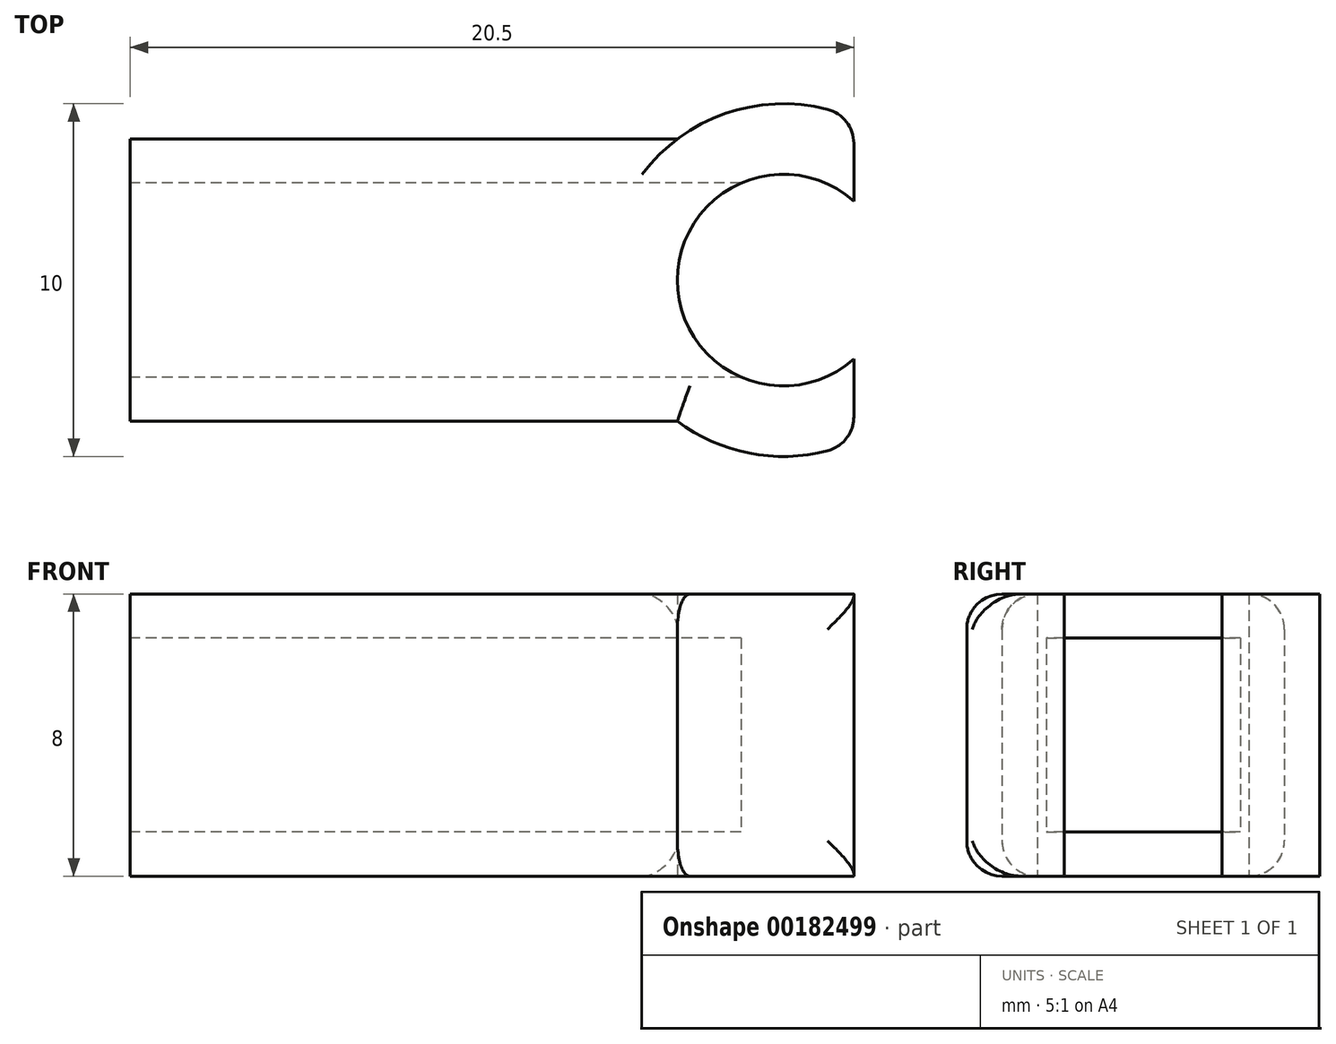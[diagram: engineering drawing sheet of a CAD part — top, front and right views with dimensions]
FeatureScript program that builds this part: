
annotation { "Feature Type Name" : "Feature", "Feature Type Description" : "" }
export const myFeature = defineFeature(function(context is Context, id is Id, definition is map)
    precondition{}
    {
        {
            var Q0;
            Q0=qCreatedBy(makeId("Top.planeOp"),FACE);
            var sketch = newSketch(context, id + "F0", { "sketchPlane" : qUnion([Q0])});
            skCircle(sketch, "E0", {"center": v(0, 0) * mm, "radius": 3 * mm});
            skCircle(sketch, "E1", {"center": v(0, 0) * mm, "radius": 5 * mm});
            skLineSegment(sketch, "E2", {"start": v(-18.5, -4) * mm, "end": v(-18.5, 4) * mm});
            skPoint(sketch, "E3", {"position": v(-10, 0) * mm});
            skLineSegment(sketch, "E4", {"start": v(2, 2.24) * mm, "end": v(2, 4.58) * mm});
            skLineSegment(sketch, "E5", {"start": v(2, -2.24) * mm, "end": v(2, -4.58) * mm});
            skLineSegment(sketch, "E6", {"start": v(-18.5, -4) * mm, "end": v(-3, -4) * mm});
            skLineSegment(sketch, "E7", {"start": v(-18.5, 4) * mm, "end": v(-3, 4) * mm});
            skLineSegment(sketch, "E8", {"start": v(-18.5, 0) * mm, "end": v(0, 0) * mm, "construction": true});
            skSolve(sketch);
        }
        {
            var Q0;
            {var subQ4=sQuery(id+"F0.wireOp",EDGE,"E4");Q0=makeQuery(id+"F0.imprint","IMPRINT",FACE,{"disambiguationData":[TD([[makeQuery(id+"F0.imprint","IMPRINT",EDGE,{"derivedFrom":subQ4}),1.0]])]});}
            var Q1;
            Q1=makeQuery(id+"F0.imprint","IMPRINT",FACE,{"disambiguationData":[TD([[makeQuery(id+"F0.imprint","IMPRINT",EDGE,{"derivedFrom":sQuery(id+"F0.wireOp",EDGE,"E2")}),-1.0]])]});
            extrude(context, id + "F1", {"entities" : qUnion([Q0, Q1]), "depth" : 8 * mm});
        }
        {
            var Q0;
            Q0=makeQuery(id+"F1.opExtrude","SWEPT_FACE",FACE,{"disambiguationData":[OSD([sQuery(id+"F0.wireOp",EDGE,"E2")])]});
            var sketch = newSketch(context, id + "F2", { "sketchPlane" : qUnion([Q0])});
            skLineSegment(sketch, "E9.bottom", {"start": v(2.75, 1.25) * mm, "end": v(-2.75, 1.25) * mm});
            skLineSegment(sketch, "E9.top", {"start": v(2.75, 6.75) * mm, "end": v(-2.75, 6.75) * mm});
            skLineSegment(sketch, "E9.left", {"start": v(2.75, 1.25) * mm, "end": v(2.75, 6.75) * mm});
            skLineSegment(sketch, "E9.right", {"start": v(-2.75, 1.25) * mm, "end": v(-2.75, 6.75) * mm});
            skPoint(sketch, "E9.middle", {"position": v(0, 4) * mm});
            skLineSegment(sketch, "E10", {"start": v(4, 8) * mm, "end": v(-4, 0) * mm, "construction": true});
            skSolve(sketch);
        }
        {
            var Q0;
            Q0=makeQuery(id+"F2.imprint","IMPRINT",FACE,{"disambiguationData":[TD([[makeQuery(id+"F2.imprint","IMPRINT",EDGE,{"derivedFrom":sQuery(id+"F2.wireOp",EDGE,"E9.bottom")}),-1.0]])]});
            extrude(context, id + "F3", {"entities" : qUnion([Q0]), "operationType" : NewBodyOperationType.REMOVE, "endBound" : BoundingType.UP_TO_NEXT, "oppositeDirection" : true, "depth" : 25 * mm});
        }
        {
            var Q0;
            Q0=makeQuery(id+"F1.opExtrude","CAP_EDGE",EDGE,{"disambiguationData":[OSD([sQuery(id+"F0.wireOp",EDGE,"rDP4hvJ2-TfQe-9iYw-sFSp-0xE8FzO6KzMa")])],"isStart":true});
            var Q1;
            Q1=makeQuery(id+"F1.opExtrude","CAP_EDGE",EDGE,{"disambiguationData":[OSD([sQuery(id+"F0.wireOp",EDGE,"rDP4hvJ2-TfQe-9iYw-sFSp-0xE8FzO6KzMa")])],"isStart":false});
            var Q2;
            Q2=makeQuery(id+"F1.opExtrude","CAP_EDGE",EDGE,{"disambiguationData":[OSD([sQuery(id+"F0.wireOp",EDGE,"h9Azr1D1-4ruZ-MHpU-PimH-VkkHi2kszzCs")])],"isStart":true});
            var Q3;
            Q3=makeQuery(id+"F1.opExtrude","CAP_EDGE",EDGE,{"disambiguationData":[OSD([sQuery(id+"F0.wireOp",EDGE,"h9Azr1D1-4ruZ-MHpU-PimH-VkkHi2kszzCs")])],"isStart":false});
            var Q4;
            Q4=makeQuery(id+"F1.opExtrude","SWEPT_EDGE",EDGE,{"disambiguationData":[OSD([sQuery(id+"F0.wireOp",EDGE,"E1"),sQuery(id+"F0.wireOp",EDGE,"E4")])]});
            var Q5;
            Q5=makeQuery(id+"F1.opExtrude","SWEPT_EDGE",EDGE,{"disambiguationData":[OSD([sQuery(id+"F0.wireOp",EDGE,"E1"),sQuery(id+"F0.wireOp",EDGE,"E5")])]});
            var Q6;
            Q6=makeQuery(id+"F1.opExtrude","CAP_EDGE",EDGE,{"disambiguationData":[OSD([sQuery(id+"F0.wireOp",EDGE,"E6")])],"isStart":true});
            var Q7;
            Q7=makeQuery(id+"F1.opExtrude","CAP_EDGE",EDGE,{"disambiguationData":[OSD([sQuery(id+"F0.wireOp",EDGE,"E7")])],"isStart":false});
            var Q8;
            Q8=makeQuery(id+"F1.opExtrude","CAP_EDGE",EDGE,{"disambiguationData":[OSD([sQuery(id+"F0.wireOp",EDGE,"E7")])],"isStart":true});
            var Q9;
            Q9=makeQuery(id+"F1.opExtrude","CAP_EDGE",EDGE,{"disambiguationData":[OSD([sQuery(id+"F0.wireOp",EDGE,"E6")])],"isStart":false});
            var Q10;
            {var subQ0=sQuery(id+"F0.wireOp",EDGE,"E1");Q10=makeQuery(id+"F1.opExtrude","CAP_EDGE",EDGE,{"disambiguationData":[OSD([subQ0]),TDD([makeQuery(id+"F0.imprint","IMPRINT",EDGE,{"disambiguationData":[TD([[makeQuery(id+"F0.imprint","INTERSECT",VERTEX,{"derivedFrom":[subQ0,sQuery(id+"F0.wireOp",EDGE,"E5")]}),1.0]])],"derivedFrom":subQ0})])],"isStart":false});}
            var Q11;
            {var subQ0=sQuery(id+"F0.wireOp",EDGE,"E1");Q11=makeQuery(id+"F1.opExtrude","CAP_EDGE",EDGE,{"disambiguationData":[OSD([subQ0]),TDD([makeQuery(id+"F0.imprint","IMPRINT",EDGE,{"disambiguationData":[TD([[makeQuery(id+"F0.imprint","INTERSECT",VERTEX,{"derivedFrom":[subQ0,sQuery(id+"F0.wireOp",EDGE,"E5")]}),1.0]])],"derivedFrom":subQ0})])],"isStart":true});}
            fillet(context, id + "F4", {"entities" : qUnion([Q0, Q1, Q2, Q3, Q4, Q5, Q6, Q7, Q8, Q9, Q10, Q11]), "radius" : 1 * mm, "tangentPropagation" : true, "allowEdgeOverflow" : false});
        }
    });
